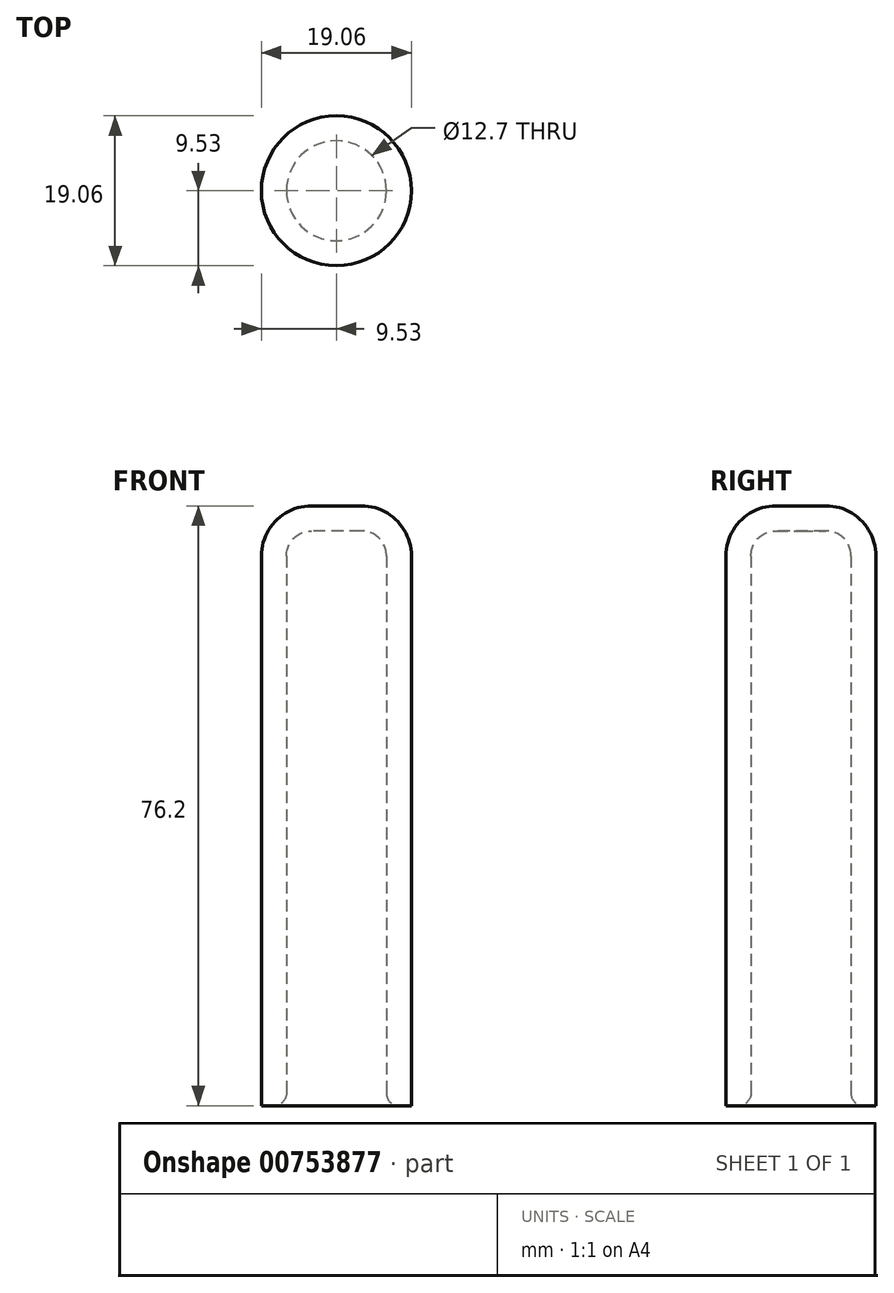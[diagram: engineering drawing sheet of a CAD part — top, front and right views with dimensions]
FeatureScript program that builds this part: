
annotation { "Feature Type Name" : "Feature", "Feature Type Description" : "" }
export const myFeature = defineFeature(function(context is Context, id is Id, definition is map)
    precondition{}
    {
        {
            var Q0;
            Q0=qCreatedBy(makeId("Top.planeOp"),FACE);
            var sketch = newSketch(context, id + "F0", { "sketchPlane" : qUnion([Q0])});
            skCircle(sketch, "E0", {"center": v(0, 0) * mm, "radius": 9.53 * mm});
            skSolve(sketch);
        }
        {
            var Q0;
            Q0 = qSketchRegion(id + "F0", true);
            extrude(context, id + "F1", {"entities" : qUnion([Q0]), "depth" : 76.2 * mm, "offsetDistance" : 25.4 * mm});
        }
        {
            var Q0;
            Q0=makeQuery(id+"F1.opExtrude","CAP_EDGE",EDGE,{"disambiguationData":[OSD([sQuery(id+"F0.wireOp",EDGE,"E0")])],"isStart":false});
            fillet(context, id + "F2", {"entities" : qUnion([Q0]), "radius" : 6.35 * mm, "tangentPropagation" : true, "allowEdgeOverflow" : false});
        }
        {
            var Q0;
            Q0=makeQuery(id+"F1.opExtrude","CAP_FACE",FACE,{"disambiguationData":[OSD([sQuery(id+"F0.wireOp",EDGE,"E0")])],"isStart":true});
            shell(context, id + "F3", {"entities" : qUnion([Q0]), "thickness" : 3.17 * mm});
        }
        {
            var Q0;
            {var subQ0=sQuery(id+"F0.wireOp",EDGE,"E0");Q0=makeQuery(id+"F3.opShell","OFFSET_EDGE",EDGE,{"disambiguationData":[OSD([subQ0]),TDD([makeQuery(id+"F1.opExtrude","CAP_EDGE",EDGE,{"disambiguationData":[OSD([subQ0])],"isStart":true})])]});}
            fillet(context, id + "F4", {"entities" : qUnion([Q0]), "radius" : 1.59 * mm, "tangentPropagation" : true, "allowEdgeOverflow" : false});
        }
    });
